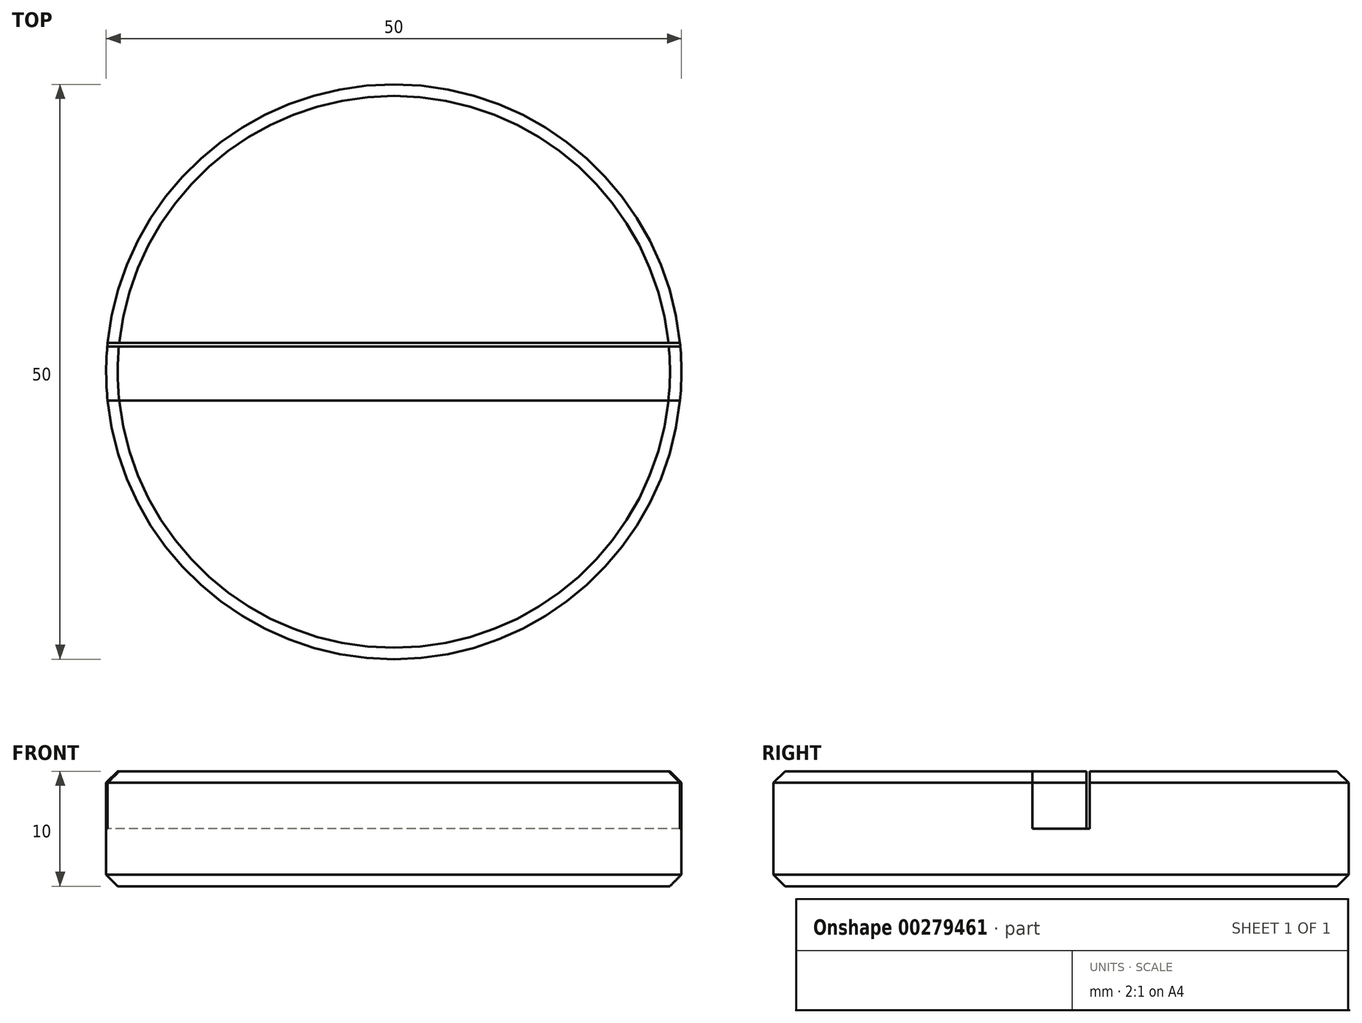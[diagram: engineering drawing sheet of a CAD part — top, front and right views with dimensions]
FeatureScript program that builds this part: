
annotation { "Feature Type Name" : "Feature", "Feature Type Description" : "" }
export const myFeature = defineFeature(function(context is Context, id is Id, definition is map)
    precondition{}
    {
        {
            var Q0;
            Q0=qCreatedBy(makeId("Top.planeOp"),FACE);
            var sketch = newSketch(context, id + "F0", { "sketchPlane" : qUnion([Q0])});
            skCircle(sketch, "E0", {"center": v(0, 0) * mm, "radius": 25 * mm});
            skLineSegment(sketch, "E1.right", {"start": v(50, -2.5) * mm, "end": v(50, 2.5) * mm});
            skLineSegment(sketch, "E2.bottom", {"start": v(-50, 2.5) * mm, "end": v(50, 2.5) * mm});
            skLineSegment(sketch, "E2.top", {"start": v(-50, -2.5) * mm, "end": v(50, -2.5) * mm});
            skLineSegment(sketch, "E2.left", {"start": v(-50, 2.5) * mm, "end": v(-50, -2.5) * mm});
            skLineSegment(sketch, "E2.right", {"start": v(50, 2.5) * mm, "end": v(50, -2.5) * mm});
            skSolve(sketch);
        }
        {
            var Q0;
            {var subQ0=sQuery(id+"F0.wireOp",EDGE,"E2.bottom");var subQ1=sQuery(id+"F0.wireOp",EDGE,"E0");var subQ2=makeQuery(id+"F0.imprint","INTERSECT",VERTEX,{"disambiguationData":[OD(0.0)],"derivedFrom":[subQ1,subQ0]});Q0=makeQuery(id+"F0.imprint","IMPRINT",FACE,{"disambiguationData":[TD([[makeQuery(id+"F0.imprint","IMPRINT",EDGE,{"disambiguationData":[TD([[subQ2,1.0]])],"derivedFrom":subQ1}),1.0]])]});}
            var Q1;
            {var subQ0=sQuery(id+"F0.wireOp",EDGE,"E2.top");var subQ1=sQuery(id+"F0.wireOp",EDGE,"E0");var subQ2=makeQuery(id+"F0.imprint","INTERSECT",VERTEX,{"disambiguationData":[OD(0.0)],"derivedFrom":[subQ1,subQ0]});Q1=makeQuery(id+"F0.imprint","IMPRINT",FACE,{"disambiguationData":[TD([[makeQuery(id+"F0.imprint","IMPRINT",EDGE,{"disambiguationData":[TD([[subQ2,-1.0]])],"derivedFrom":subQ1}),1.0]])]});}
            var Q2;
            {var subQ0=sQuery(id+"F0.wireOp",EDGE,"E2.bottom");var subQ1=sQuery(id+"F0.wireOp",EDGE,"E0");var subQ2=makeQuery(id+"F0.imprint","INTERSECT",VERTEX,{"disambiguationData":[OD(0.0)],"derivedFrom":[subQ1,subQ0]});Q2=makeQuery(id+"F0.imprint","IMPRINT",FACE,{"disambiguationData":[TD([[makeQuery(id+"F0.imprint","IMPRINT",EDGE,{"disambiguationData":[TD([[subQ2,-1.0]])],"derivedFrom":subQ1}),1.0]])]});}
            extrude(context, id + "F1", {"entities" : qUnion([Q0, Q1, Q2]), "depth" : 5 * mm});
        }
        {
            var Q0;
            {var subQ0=sQuery(id+"F0.wireOp",EDGE,"E2.top");var subQ1=sQuery(id+"F0.wireOp",EDGE,"E0");var subQ2=makeQuery(id+"F0.imprint","INTERSECT",VERTEX,{"disambiguationData":[OD(0.0)],"derivedFrom":[subQ1,subQ0]});Q0=makeQuery(id+"F0.imprint","IMPRINT",FACE,{"disambiguationData":[TD([[makeQuery(id+"F0.imprint","IMPRINT",EDGE,{"disambiguationData":[TD([[subQ2,-1.0]])],"derivedFrom":subQ1}),1.0]])]});}
            var Q1;
            {var subQ0=sQuery(id+"F0.wireOp",EDGE,"E2.bottom");var subQ1=sQuery(id+"F0.wireOp",EDGE,"E0");var subQ2=makeQuery(id+"F0.imprint","INTERSECT",VERTEX,{"disambiguationData":[OD(0.0)],"derivedFrom":[subQ1,subQ0]});Q1=makeQuery(id+"F0.imprint","IMPRINT",FACE,{"disambiguationData":[TD([[makeQuery(id+"F0.imprint","IMPRINT",EDGE,{"disambiguationData":[TD([[subQ2,1.0]])],"derivedFrom":subQ1}),1.0]])]});}
            extrude(context, id + "F2", {"entities" : qUnion([Q0, Q1]), "operationType" : NewBodyOperationType.ADD, "depth" : 10 * mm});
        }
        {
            var Q0;
            Q0=makeQuery(id+"F1.opExtrude","CAP_EDGE",EDGE,{"disambiguationData":[OSD([sQuery(id+"F0.wireOp",EDGE,"E0")])],"isStart":true});
            var Q1;
            Q1=makeQuery(id+"F2.opExtrude","CAP_EDGE",EDGE,{"disambiguationData":[OSD([sQuery(id+"F0.wireOp",EDGE,"E0")])],"isStart":false});
            chamfer(context, id + "F3", {"entities" : qUnion([Q0, Q1]), "width" : 1 * mm, "tangentPropagation" : true});
        }
        {
            var Q0;
            Q0=makeQuery(id+"F1.opExtrude","CAP_FACE",FACE,{"disambiguationData":[OSD([sQuery(id+"F0.wireOp",EDGE,"E0")])],"isStart":false});
            var sketch = newSketch(context, id + "F4", { "sketchPlane" : qUnion([Q0])});
            skLineSegment(sketch, "E3.0.0", {"start": v(-24.87, 2.5) * mm, "end": v(-24.87, 2.5) * mm});
            skLineSegment(sketch, "E3.0.1", {"start": v(-24.87, 2.5) * mm, "end": v(-24.87, 2.5) * mm});
            skLineSegment(sketch, "E3.0.2", {"start": v(-24.87, 2.5) * mm, "end": v(-24.87, 2.5) * mm});
            skLineSegment(sketch, "E3.0.3", {"start": v(-24.87, 2.5) * mm, "end": v(-24.87, 2.5) * mm});
            skLineSegment(sketch, "E4.0", {"start": v(10.3, 2.2) * mm, "end": v(-24.9, 2.2) * mm});
            skLineSegment(sketch, "E4.1", {"start": v(10.3, 2.2) * mm, "end": v(2.5, 2.2) * mm});
            skLineSegment(sketch, "E4.2", {"start": v(24.9, 2.2) * mm, "end": v(2.5, 2.2) * mm});
            skSolve(sketch);
        }
        {
            var Q0;
            {var subQ2=sQuery(id+"F4.wireOp",EDGE,"E4.0");Q0=makeQuery(id+"F4.imprint","IMPRINT",FACE,{"disambiguationData":[TD([[makeQuery(id+"F4.imprint","IMPRINT",EDGE,{"derivedFrom":subQ2}),1.0]])]});}
            extrude(context, id + "F5", {"entities" : qUnion([Q0]), "depth" : 5 * mm});
        }
        {
            var Q0;
            {var subQ0=sQuery(id+"F0.wireOp",EDGE,"E0");var subQ1=makeQuery(id+"F2.boolean.opBoolean","SPLIT",EDGE,{"disambiguationData":[OD(0.0)],"derivedFrom":makeQuery(id+"F1.opExtrude","CAP_EDGE",EDGE,{"disambiguationData":[OSD([subQ0])],"isStart":false})});Q0=makeQuery(id+"F5.opExtrude","CAP_EDGE",EDGE,{"disambiguationData":[OSD([subQ0]),TDD([makeQuery(id+"F4.imprint","IMPRINT",EDGE,{"disambiguationData":[TD([[makeQuery(id+"F4.imprint","INTERSECT",VERTEX,{"derivedFrom":[subQ1,sQuery(id+"F4.wireOp",EDGE,"E4.0")]}),-1.0]])],"derivedFrom":subQ1})])],"isStart":false});}
            var Q1;
            {var subQ0=sQuery(id+"F0.wireOp",EDGE,"E0");var subQ1=makeQuery(id+"F2.boolean.opBoolean","SPLIT",EDGE,{"disambiguationData":[OD(1.0)],"derivedFrom":makeQuery(id+"F1.opExtrude","CAP_EDGE",EDGE,{"disambiguationData":[OSD([subQ0])],"isStart":false})});Q1=makeQuery(id+"F5.opExtrude","CAP_EDGE",EDGE,{"disambiguationData":[OSD([subQ0]),TDD([makeQuery(id+"F4.imprint","IMPRINT",EDGE,{"disambiguationData":[TD([[makeQuery(id+"F4.imprint","INTERSECT",VERTEX,{"derivedFrom":[subQ1,sQuery(id+"F4.wireOp",EDGE,"E4.2")]}),1.0]])],"derivedFrom":subQ1})])],"isStart":false});}
            chamfer(context, id + "F6", {"entities" : qUnion([Q0, Q1]), "width" : 1 * mm, "tangentPropagation" : true});
        }
    });
